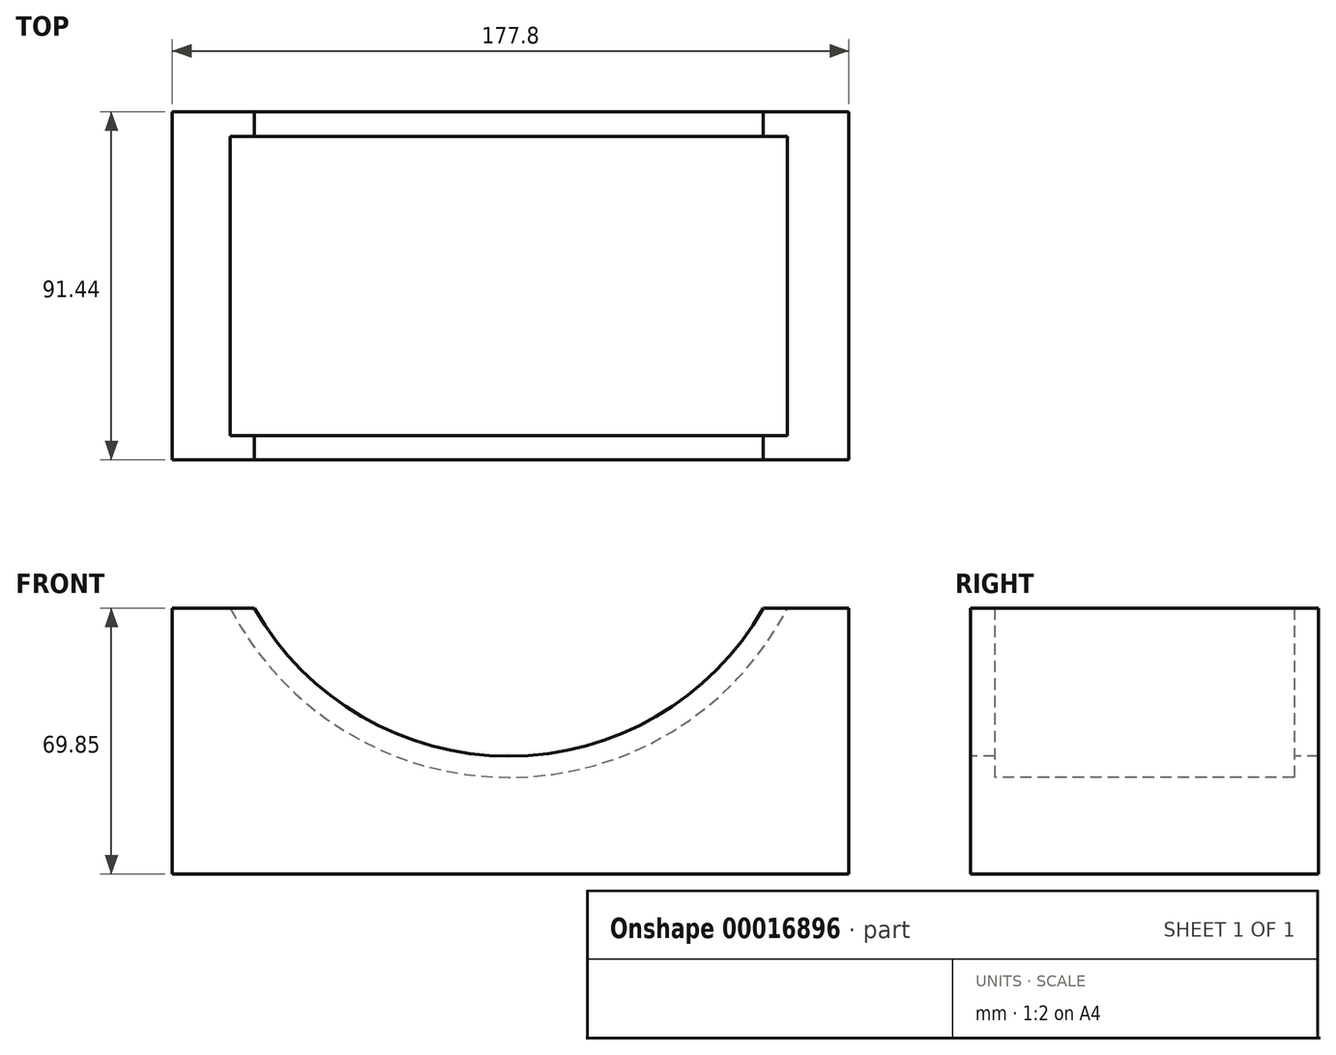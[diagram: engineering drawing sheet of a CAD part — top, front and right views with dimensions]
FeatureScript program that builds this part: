
annotation { "Feature Type Name" : "Feature", "Feature Type Description" : "" }
export const myFeature = defineFeature(function(context is Context, id is Id, definition is map)
    precondition{}
    {
        {
            var Q0;
            Q0=qCreatedBy(makeId("Top.planeOp"),FACE);
            var sketch = newSketch(context, id + "F0", { "sketchPlane" : qUnion([Q0])});
            skLineSegment(sketch, "E0.bottom", {"start": v(-63.02, 43.25) * mm, "end": v(114.78, 43.25) * mm});
            skLineSegment(sketch, "E0.top", {"start": v(-63.02, -48.2) * mm, "end": v(114.78, -48.2) * mm});
            skLineSegment(sketch, "E0.left", {"start": v(-63.02, 43.25) * mm, "end": v(-63.02, -48.2) * mm});
            skLineSegment(sketch, "E0.right", {"start": v(114.78, 43.25) * mm, "end": v(114.78, -48.2) * mm});
            skSolve(sketch);
        }
        {
            var Q0;
            Q0=makeQuery(id+"F0.imprint","IMPRINT",FACE,{"disambiguationData":[TD([[makeQuery(id+"F0.imprint","IMPRINT",EDGE,{"derivedFrom":sQuery(id+"F0.wireOp",EDGE,"E0.bottom")}),-1.0]])]});
            extrude(context, id + "F1", {"entities" : qUnion([Q0]), "depth" : 69.85 * mm});
        }
        {
            var Q0;
            Q0=makeQuery(id+"F1.opExtrude","SWEPT_FACE",FACE,{"disambiguationData":[OSD([sQuery(id+"F0.wireOp",EDGE,"E0.top")])]});
            var sketch = newSketch(context, id + "F2", { "sketchPlane" : qUnion([Q0])});
            skArc(sketch, "E1", {"start": v(-47.78, 69.85) * mm, "mid": v(25.45, 25.4) * mm, "end": v(98.68, 69.85) * mm});
            skLineSegment(sketch, "E2", {"start": v(98.68, 69.85) * mm, "end": v(-47.78, 69.85) * mm});
            skSolve(sketch);
        }
        {
            var Q0;
            Q0=makeQuery(id+"F2.imprint","IMPRINT",FACE,{"disambiguationData":[TD([[makeQuery(id+"F2.imprint","IMPRINT",EDGE,{"derivedFrom":sQuery(id+"F2.wireOp",EDGE,"E1")}),1.0]])]});
            extrude(context, id + "F3", {"entities" : qUnion([Q0]), "operationType" : NewBodyOperationType.REMOVE, "oppositeDirection" : true, "depth" : 85.03 * mm, "hasSecondDirection" : true, "secondDirectionOppositeDirection" : true, "secondDirectionDepth" : 6.35 * mm});
        }
        {
            var Q0;
            Q0=makeQuery(id+"F1.opExtrude","SWEPT_FACE",FACE,{"disambiguationData":[OSD([sQuery(id+"F0.wireOp",EDGE,"E0.top")])]});
            var sketch = newSketch(context, id + "F4", { "sketchPlane" : qUnion([Q0])});
            skArc(sketch, "E3", {"start": v(-41.43, 69.85) * mm, "mid": v(25.45, 30.98) * mm, "end": v(92.33, 69.85) * mm});
            skLineSegment(sketch, "E4", {"start": v(-41.43, 69.85) * mm, "end": v(92.33, 69.85) * mm});
            skSolve(sketch);
        }
        {
            var Q0;
            Q0=makeQuery(id+"F4.imprint","IMPRINT",FACE,{"disambiguationData":[TD([[makeQuery(id+"F4.imprint","IMPRINT",EDGE,{"derivedFrom":sQuery(id+"F4.wireOp",EDGE,"E3")}),1.0]])]});
            extrude(context, id + "F5", {"entities" : qUnion([Q0]), "operationType" : NewBodyOperationType.REMOVE, "oppositeDirection" : true, "depth" : 107.15 * mm});
        }
    });
